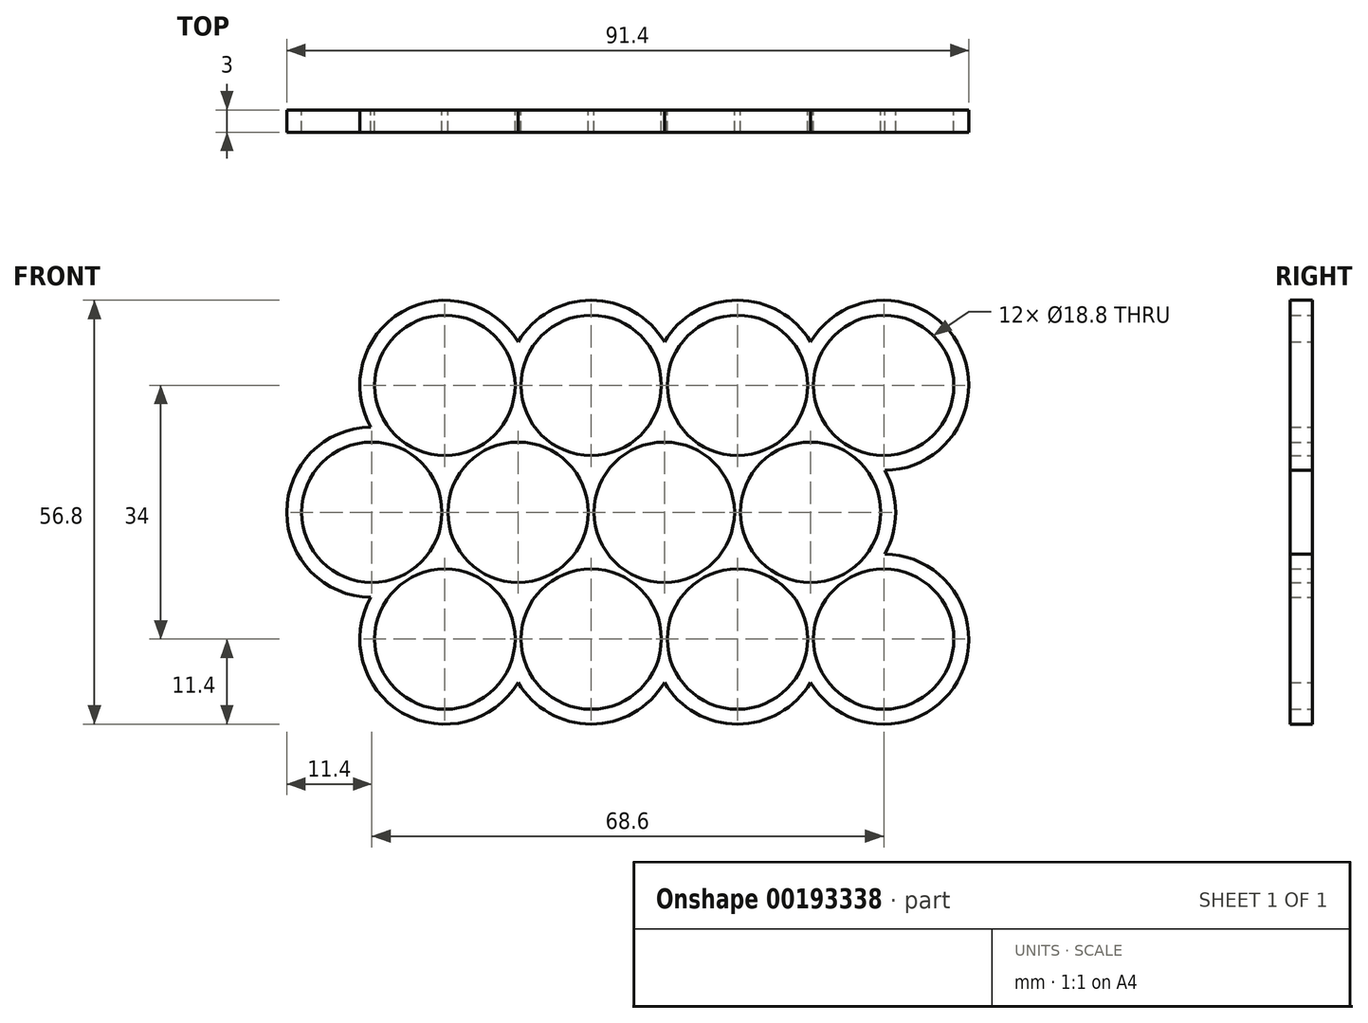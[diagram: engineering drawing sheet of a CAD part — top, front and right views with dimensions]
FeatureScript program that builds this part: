
annotation { "Feature Type Name" : "Feature", "Feature Type Description" : "" }
export const myFeature = defineFeature(function(context is Context, id is Id, definition is map)
    precondition{}
    {
        {
            var Q0;
            Q0=qCreatedBy(makeId("Front.planeOp"),FACE);
            var sketch = newSketch(context, id + "F0", { "sketchPlane" : qUnion([Q0])});
            skCircle(sketch, "E0.1.0.0", {"center": v(19.6, 0) * mm, "radius": 9.4 * mm});
            skCircle(sketch, "E0.2.0.0", {"center": v(39.2, 0) * mm, "radius": 9.4 * mm});
            skArc(sketch, "E0.3.0.0", {"start": v(58.8, 9.4) * mm, "mid": v(54.1, -8.14) * mm, "end": v(66.94, 4.7) * mm});
            skLineSegment(sketch, "E0.direction1", {"start": v(0, 0) * mm, "end": v(19.6, 0) * mm, "construction": true});
            skLineSegment(sketch, "E1", {"start": v(0, -17) * mm, "end": v(73.2, -17) * mm, "construction": true});
            skLineSegment(sketch, "E2", {"start": v(9.8, 0) * mm, "end": v(9.8, -17) * mm, "construction": true});
            skCircle(sketch, "E3", {"center": v(9.8, -17) * mm, "radius": 9.4 * mm});
            skCircle(sketch, "E4.1.0.0", {"center": v(29.4, -17) * mm, "radius": 9.4 * mm});
            skCircle(sketch, "E4.2.0.0", {"center": v(49, -17) * mm, "radius": 9.4 * mm});
            skCircle(sketch, "E4.3.0.0", {"center": v(68.6, -17) * mm, "radius": 9.4 * mm});
            skLineSegment(sketch, "E4.direction1", {"start": v(9.8, -17) * mm, "end": v(29.4, -17) * mm, "construction": true});
            skLineSegment(sketch, "E5", {"start": v(9.8, -17) * mm, "end": v(9.8, -26.4) * mm, "construction": true});
            skLineSegment(sketch, "E6", {"start": v(68.6, -17) * mm, "end": v(68.6, -26.4) * mm, "construction": true});
            skArc(sketch, "E7", {"start": v(58.8, 9.4) * mm, "mid": v(63.5, 8.14) * mm, "end": v(66.94, 4.7) * mm});
            skArc(sketch, "E8", {"start": v(76.74, -12.3) * mm, "mid": v(76.74, -21.7) * mm, "end": v(68.6, -26.4) * mm});
            skArc(sketch, "E9", {"start": v(9.8, -26.4) * mm, "mid": v(5.1, -25.14) * mm, "end": v(1.66, -21.7) * mm});
            skArc(sketch, "E10.trimOffspring", {"start": v(9.8, -5.82) * mm, "mid": v(9.87, -5.71) * mm, "end": v(9.93, -5.6) * mm});
            skArc(sketch, "E11.trimOffspring", {"start": v(9.93, -5.6) * mm, "mid": v(9.86, -5.6) * mm, "end": v(9.8, -5.6) * mm});
            skCircle(sketch, "E12.0.4.0", {"center": v(78.4, 0) * mm, "radius": 9.4 * mm});
            skLineSegment(sketch, "E13", {"start": v(0, 0) * mm, "end": v(9.8, -17) * mm, "construction": true});
            skCircle(sketch, "E14.1.0.0", {"center": v(19.6, -34) * mm, "radius": 9.4 * mm});
            skLineSegment(sketch, "E14.direction1", {"start": v(9.8, -17) * mm, "end": v(19.6, -34) * mm, "construction": true});
            skCircle(sketch, "E15.1.0.0", {"center": v(39.2, -34) * mm, "radius": 9.4 * mm});
            skCircle(sketch, "E15.2.0.0", {"center": v(58.8, -34) * mm, "radius": 9.4 * mm});
            skCircle(sketch, "E15.3.0.0", {"center": v(78.4, -34) * mm, "radius": 9.4 * mm});
            skLineSegment(sketch, "E15.direction1", {"start": v(19.6, -34) * mm, "end": v(39.2, -34) * mm, "construction": true});
            skPoint(sketch, "E16.start.orphan", {"position": v(0, 9.4) * mm});
            skArc(sketch, "E17.0", {"start": v(29.4, 5.82) * mm, "mid": v(13.78, 9.8) * mm, "end": v(9.8, -5.82) * mm});
            skArc(sketch, "E18.0", {"start": v(58.8, 11.4) * mm, "mid": v(64.5, 9.87) * mm, "end": v(68.68, 5.7) * mm});
            skArc(sketch, "E18.1", {"start": v(58.8, 11.4) * mm, "mid": v(53.16, 9.9) * mm, "end": v(49, 5.82) * mm});
            skArc(sketch, "E19.0", {"start": v(9.67, -28.4) * mm, "mid": v(13.89, -43.87) * mm, "end": v(29.4, -39.82) * mm});
            skArc(sketch, "E20.trimOffspring", {"start": v(49, 5.82) * mm, "mid": v(39.2, 11.4) * mm, "end": v(29.4, 5.82) * mm});
            skArc(sketch, "E21.trimOffspring", {"start": v(9.93, -5.6) * mm, "mid": v(-1.6, -16.87) * mm, "end": v(9.67, -28.4) * mm});
            skArc(sketch, "E22.trimOffspring", {"start": v(78.53, -11.4) * mm, "mid": v(88.28, 5.7) * mm, "end": v(68.6, 5.82) * mm});
            skArc(sketch, "E23.trimOffspring", {"start": v(78.53, -22.6) * mm, "mid": v(80, -17) * mm, "end": v(78.53, -11.4) * mm});
            skArc(sketch, "E24.trimOffspring", {"start": v(68.6, -39.82) * mm, "mid": v(88.28, -39.7) * mm, "end": v(78.53, -22.6) * mm});
            skArc(sketch, "E25.trimOffspring", {"start": v(49, -39.82) * mm, "mid": v(58.8, -45.4) * mm, "end": v(68.6, -39.82) * mm});
            skArc(sketch, "E26.trimOffspring", {"start": v(29.4, -39.82) * mm, "mid": v(39.2, -45.4) * mm, "end": v(49, -39.82) * mm});
            skSolve(sketch);
        }
        {
            var Q0;
            Q0=qSketchRegion(id+"F0",true);
            var Q1;
            {var subQ3=sQuery(id+"F0.wireOp",EDGE,"E0.1.0.0");Q1=makeQuery(id+"F0.imprint","IMPRINT",FACE,{"disambiguationData":[TD([[makeQuery(id+"F0.imprint","IMPRINT",EDGE,{"derivedFrom":subQ3}),-1.0]])]});}
            extrude(context, id + "F1", {"entities" : qUnion([Q0, Q1]), "depth" : 3 * mm});
        }
    });
